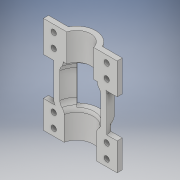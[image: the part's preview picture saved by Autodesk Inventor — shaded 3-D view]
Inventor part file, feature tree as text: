
AUTODESK INVENTOR PART (.ipt)
format: ipt  version: 2018 (Build 220112000, 112)  size: 345,088 bytes
history: native  units: in
note: dims shown in document units (in); Inventor stores cm internally (conversion verified against a paired STEP export)
features: fillet x6, extrude x5, sketch x5, mirror x1, projected_geometry x1
ambient origin geometry x8: Origin, YZ Plane, XZ Plane, XY Plane, X Axis, Y Axis, Z Axis, Center Point
bodies: Solid1 (feature_tree)
feature tree (18):
  extrude  "Extrusion1"  Depth=0.1875in
  extrude  "Extrusion2"  Depth=0.1875in
  extrude  "Extrusion3"  Depth=1.5in TaperAngle=0.0deg
  extrude  "Extrusion4"  Depth=0.1875in
  fillet  "Fillet1"  Radius=0.5in
  fillet  "Fillet3"  Radius=1.0in
  fillet  "Fillet4"  Radius=0.25in
  fillet  "Fillet5"  Radius=0.25in
  fillet  "Fillet6"  Radius=0.25in
  fillet  "Fillet7"  Radius=0.25in
  extrude  "Extrusion5"  Depth=0.25in
  mirror  "Mirror1"
  sketch  "Sketch1"  dims[d18=1.19in d19=0.1875in]
  sketch  "Sketch2"  dims[d20=0.1875in d21=0.75in d23=0.1875in]
  sketch  "Sketch3"  dims[d24=1.0in d25=0.0in d33=1.5in d34=0.0in]
  sketch  "Sketch4"  dims[d35=0.1875in d36=0.1875in d37=0.5in d39=1.0in d40=0.0in d41=0.25in d42=0.0in d43=0.25in d45=0.25in d46=0.25in]
  projected_geometry  "Projected Loop1"
  sketch  "Sketch5"  dims[d47=0.25in d48=0.25in d49=0.25in d50=0.375in d51=0.375in d52=0.25in d53=0.25in d54=0.25in d55=0.25in d56=0.375in d57=0.375in d58=0.1935in d59=0.75in d60=0.0in d61=0.7825in d62=0.125in d63=0.6875in d64=0.125in d65=0.75in d66=0.9647in]
